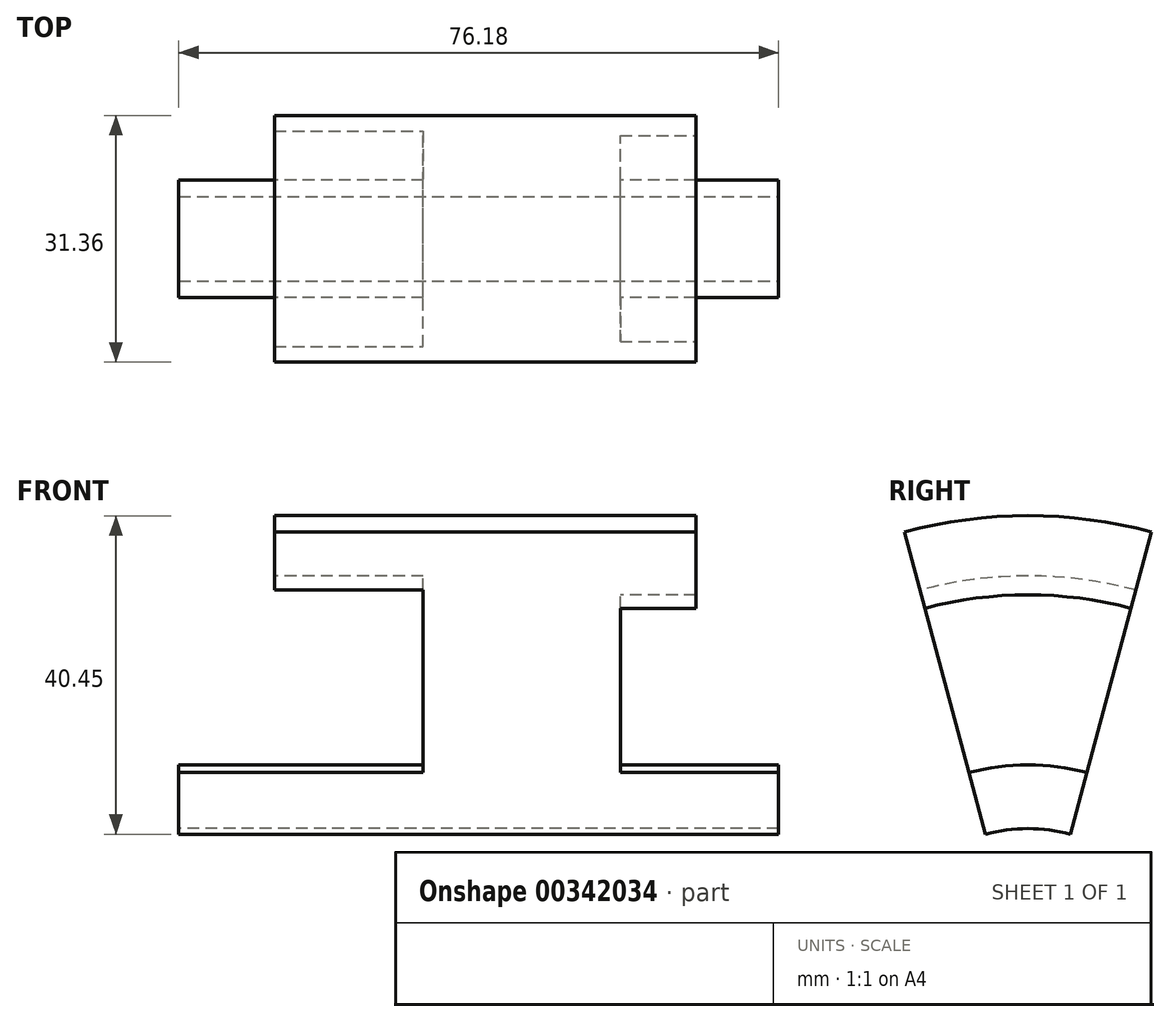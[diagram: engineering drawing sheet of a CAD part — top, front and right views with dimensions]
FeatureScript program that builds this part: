
annotation { "Feature Type Name" : "Feature", "Feature Type Description" : "" }
export const myFeature = defineFeature(function(context is Context, id is Id, definition is map)
    precondition{}
    {
        {
            var Q0;
            Q0=qCreatedBy(makeId("Front.planeOp"),FACE);
            var sketch = newSketch(context, id + "F0", { "sketchPlane" : qUnion([Q0])});
            skLineSegment(sketch, "E0", {"start": v(-89.24, 0) * mm, "end": v(92.84, 0) * mm, "construction": true});
            skLineSegment(sketch, "E1", {"start": v(-38.1, 20.85) * mm, "end": v(38.1, 20.85) * mm});
            skLineSegment(sketch, "E2", {"start": v(38.1, 20.85) * mm, "end": v(38.1, 28.95) * mm});
            skLineSegment(sketch, "E3", {"start": v(38.1, 28.95) * mm, "end": v(18, 28.95) * mm});
            skLineSegment(sketch, "E4", {"start": v(18, 28.95) * mm, "end": v(18, 50.54) * mm});
            skLineSegment(sketch, "E5", {"start": v(18, 50.54) * mm, "end": v(27.6, 50.54) * mm});
            skLineSegment(sketch, "E6", {"start": v(27.6, 50.54) * mm, "end": v(27.6, 60.6) * mm});
            skLineSegment(sketch, "E7", {"start": v(27.6, 60.6) * mm, "end": v(-25.95, 60.6) * mm});
            skLineSegment(sketch, "E8", {"start": v(-25.95, 60.6) * mm, "end": v(-25.95, 52.94) * mm});
            skLineSegment(sketch, "E9", {"start": v(-25.95, 52.94) * mm, "end": v(-7.05, 52.94) * mm});
            skLineSegment(sketch, "E10", {"start": v(-7.05, 52.94) * mm, "end": v(-7.05, 28.95) * mm});
            skLineSegment(sketch, "E11", {"start": v(-7.05, 28.95) * mm, "end": v(-38.1, 28.95) * mm});
            skLineSegment(sketch, "E12", {"start": v(-38.1, 28.95) * mm, "end": v(-38.1, 20.85) * mm});
            skLineSegment(sketch, "E13", {"start": v(0, 0) * mm, "end": v(0, 92.54) * mm, "construction": true});
            skSolve(sketch);
        }
        {
            var Q0;
            Q0 = qSketchRegion(id + "F0", true);
            var Q1;
            Q1=sQuery(id+"F0.wireOp",EDGE,"E0");
            revolve(context, id + "F1", {"entities" : qUnion([Q0]), "axis" : qUnion([Q1]), "revolveType" : RevolveType.SYMMETRIC, "angle" : 30 * degree});
        }
    });
